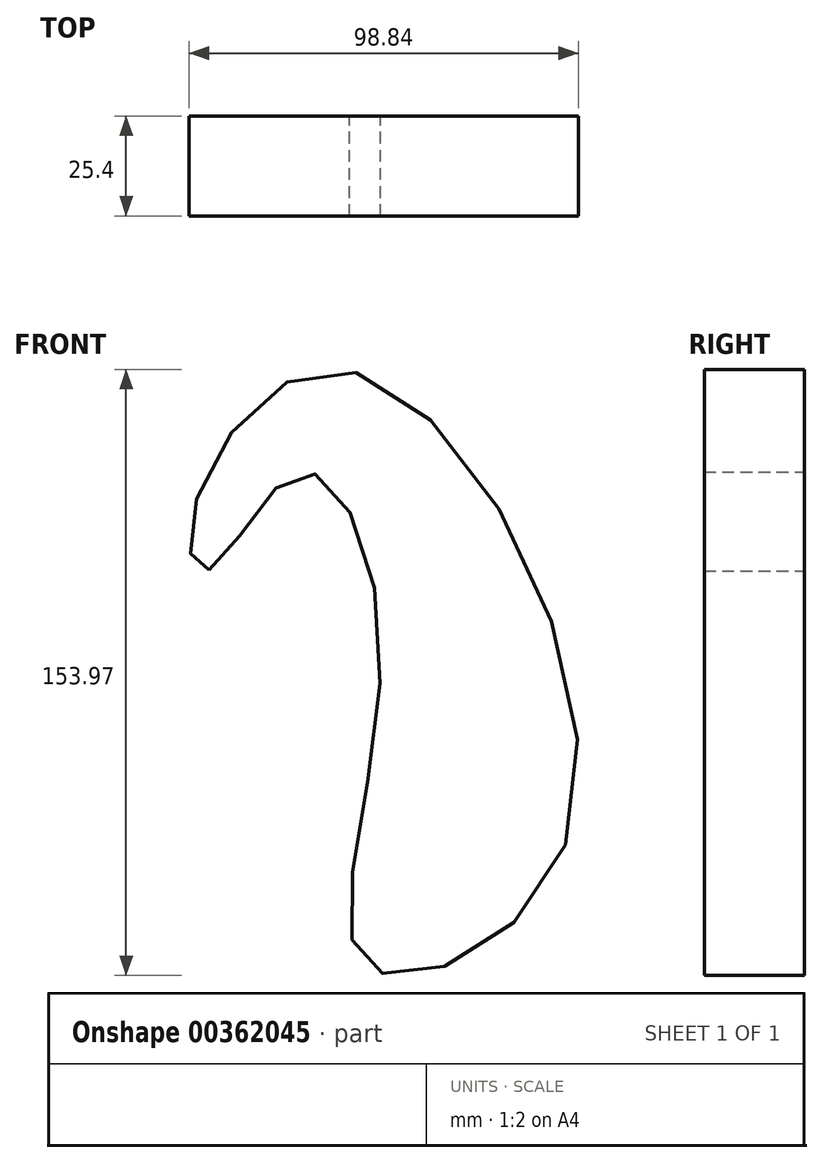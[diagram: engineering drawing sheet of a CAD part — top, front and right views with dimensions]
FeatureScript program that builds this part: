
annotation { "Feature Type Name" : "Feature", "Feature Type Description" : "" }
export const myFeature = defineFeature(function(context is Context, id is Id, definition is map)
    precondition{}
    {
        {
            var Q0;
            Q0=qCreatedBy(makeId("Front.planeOp"),FACE);
            var sketch = newSketch(context, id + "F0", { "sketchPlane" : qUnion([Q0])});
            skFitSpline(sketch, "E0", {"points": [v(-36.26, -6.47) * mm, v(-13.7, 18.16) * mm, v(7.34, -28.17) * mm, v(4.05, -107.18) * mm, v(55.28, -73.26) * mm, v(-2.43, 44.34) * mm, v(-41.15, 3.81) * mm, v(-36.26, -6.47) * mm]});
            skSolve(sketch);
        }
        {
            var Q0;
            Q0 = qSketchRegion(id + "F0", true);
            extrude(context, id + "F1", {"entities" : qUnion([Q0]), "depth" : 25.4 * mm});
        }
    });
